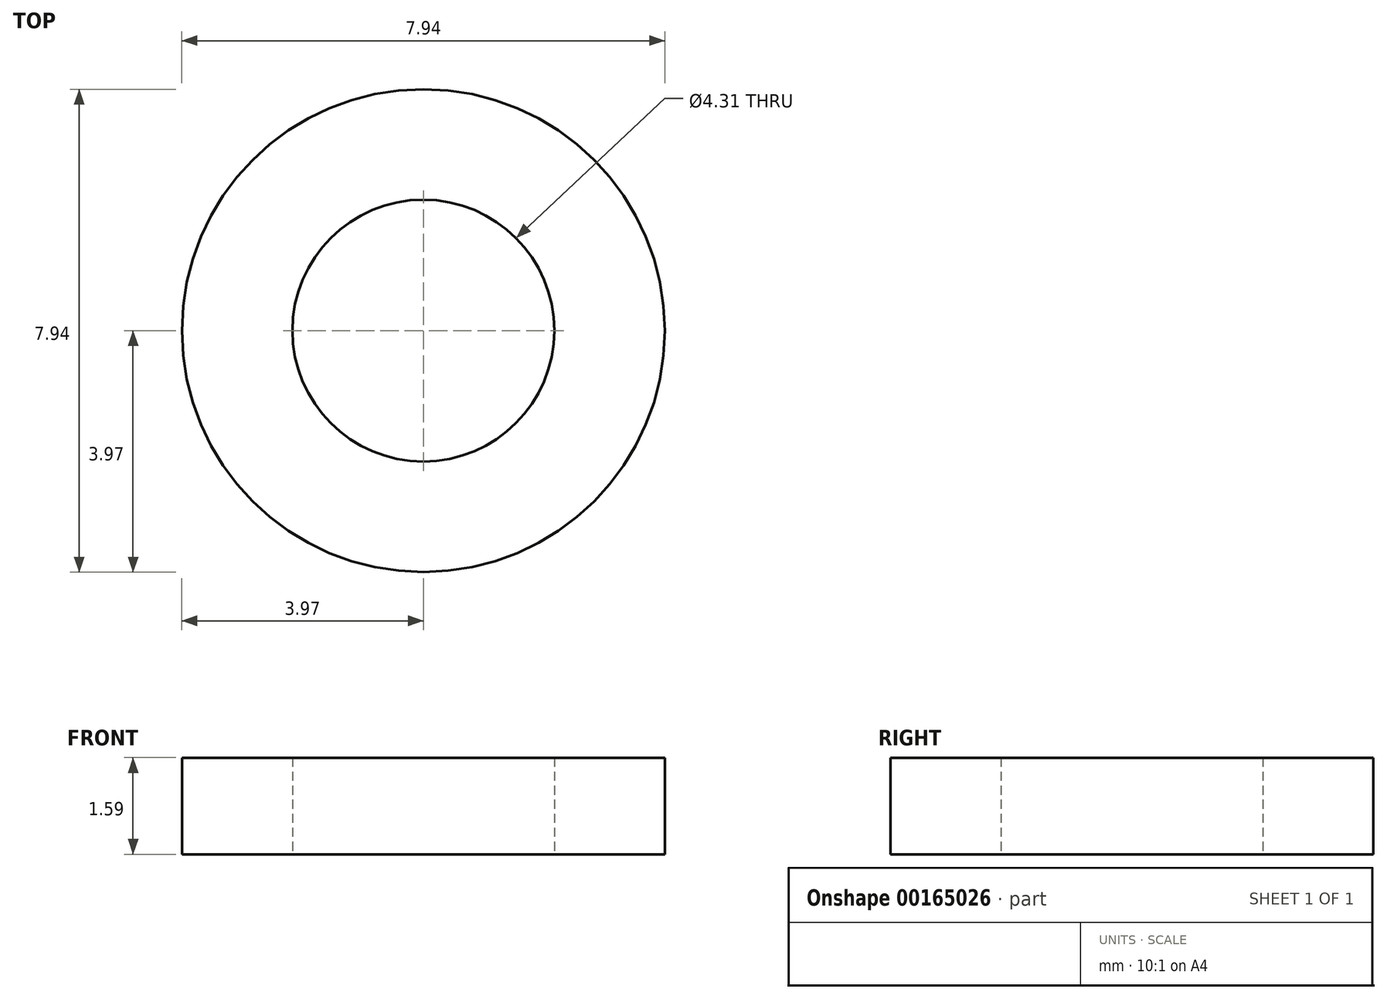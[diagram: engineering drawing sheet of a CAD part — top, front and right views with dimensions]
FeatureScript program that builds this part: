
annotation { "Feature Type Name" : "Feature", "Feature Type Description" : "" }
export const myFeature = defineFeature(function(context is Context, id is Id, definition is map)
    precondition{}
    {
        {
            var Q0;
            Q0=qCreatedBy(makeId("Top.planeOp"),FACE);
            var sketch = newSketch(context, id + "F0", { "sketchPlane" : qUnion([Q0])});
            skCircle(sketch, "E0", {"center": v(0, 0) * mm, "radius": 2.15 * mm});
            skCircle(sketch, "E1", {"center": v(0, 0) * mm, "radius": 3.97 * mm});
            skSolve(sketch);
        }
        {
            var Q0;
            Q0 = qSketchRegion(id + "F0", true);
            extrude(context, id + "F1", {"entities" : qUnion([Q0]), "depth" : 1.59 * mm});
        }
    });
